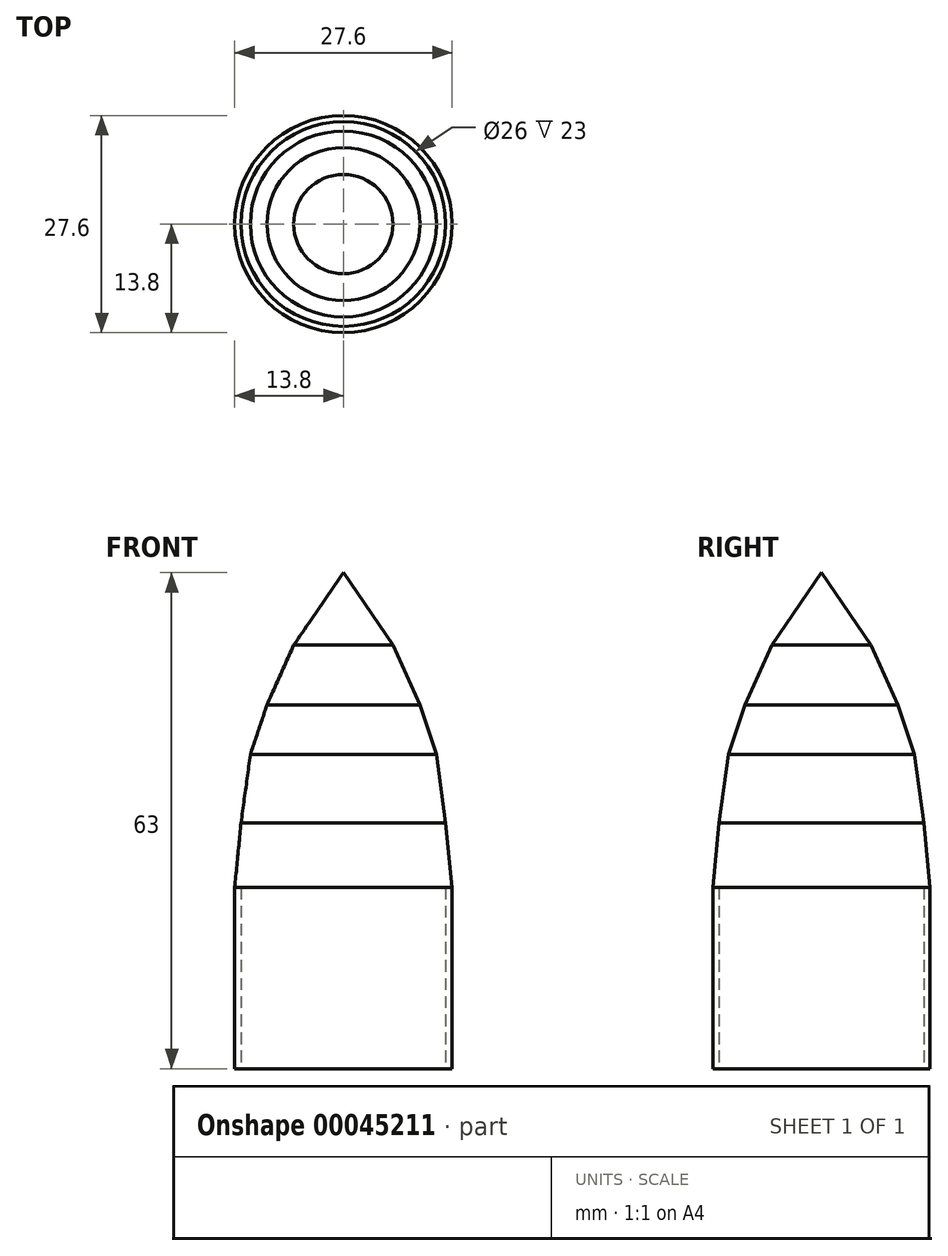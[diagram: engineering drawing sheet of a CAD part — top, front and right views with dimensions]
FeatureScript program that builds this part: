
annotation { "Feature Type Name" : "Feature", "Feature Type Description" : "" }
export const myFeature = defineFeature(function(context is Context, id is Id, definition is map)
    precondition{}
    {
        {
            var Q0;
            Q0=qCreatedBy(makeId("Front.planeOp"),FACE);
            var sketch = newSketch(context, id + "F0", { "sketchPlane" : qUnion([Q0])});
            skLineSegment(sketch, "E0", {"start": v(-13, 0) * mm, "end": v(-13, 23) * mm});
            skLineSegment(sketch, "E1", {"start": v(-13, 23) * mm, "end": v(-13.8, 23) * mm});
            skLineSegment(sketch, "E2", {"start": v(-13.8, 23) * mm, "end": v(-13.8, 0) * mm});
            skLineSegment(sketch, "E3", {"start": v(-13.8, 23) * mm, "end": v(-13, 31.24) * mm});
            skLineSegment(sketch, "E4", {"start": v(-13, 31.24) * mm, "end": v(-11.81, 39.9) * mm});
            skLineSegment(sketch, "E5", {"start": v(-11.81, 39.9) * mm, "end": v(-9.71, 46.2) * mm});
            skLineSegment(sketch, "E6", {"start": v(-9.71, 46.2) * mm, "end": v(-6.3, 53.81) * mm});
            skLineSegment(sketch, "E7", {"start": v(-6.3, 53.81) * mm, "end": v(0, 63) * mm});
            skLineSegment(sketch, "E8", {"start": v(-13.8, 23) * mm, "end": v(0, 23) * mm});
            skLineSegment(sketch, "E9", {"start": v(0, 23) * mm, "end": v(0, 63) * mm});
            skLineSegment(sketch, "E10", {"start": v(0, -25.46) * mm, "end": v(0, 75.08) * mm});
            skLineSegment(sketch, "E11", {"start": v(-13.8, 0) * mm, "end": v(-13, 0) * mm});
            skSolve(sketch);
        }
        {
            var Q0;
            {var subQ0=sQuery(id+"F0.wireOp",EDGE,"E3");Q0=makeQuery(id+"F0.imprint","IMPRINT",FACE,{"disambiguationData":[TD([[makeQuery(id+"F0.imprint","IMPRINT",EDGE,{"derivedFrom":subQ0}),-1.0]])]});}
            var Q1;
            {var subQ0=sQuery(id+"F0.wireOp",EDGE,"E0");Q1=makeQuery(id+"F0.imprint","IMPRINT",FACE,{"disambiguationData":[TD([[makeQuery(id+"F0.imprint","IMPRINT",EDGE,{"derivedFrom":subQ0}),1.0]])]});}
            var Q2;
            Q2=sQuery(id+"F0.wireOp",EDGE,"E10");
            revolve(context, id + "F1", {"entities" : qUnion([Q0, Q1]), "axis" : qUnion([Q2]), "revolveType" : RevolveType.FULL});
        }
    });
